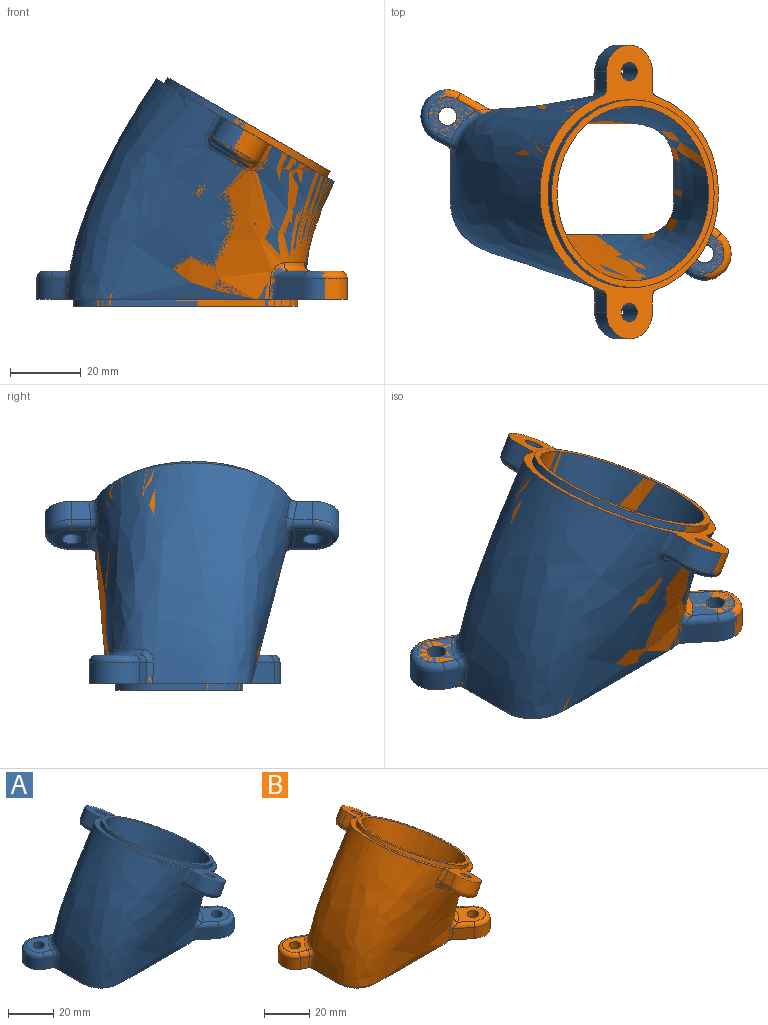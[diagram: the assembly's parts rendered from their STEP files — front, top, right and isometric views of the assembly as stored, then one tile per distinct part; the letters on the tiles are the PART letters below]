
ASSEMBLY  parts=2 mates=1
PART A: 60 faces, bbox 97.4x92.8x76.8 mm
  f0: plane 53.03x45.93mm, normal (0.5,0,0.87), area 293.8mm2, adj f11,f27
  f1: bspline ~76.16x63.21mm, area 8862.1mm2, adj f24,f26,f34,f35,f36,f37,f38,f39
  f2: plane 5.83x5.2mm, normal (0.87,0,-0.5), area 30.9mm2, adj f4,f26,f49,f54
  f3: plane 5.36x5.2mm, normal (-0.87,0,0.5), area 29mm2, adj f4,f26,f47,f50
  f4: cylinder r=7.5mm len=15.99mm, axis (0.5,0,0.87), area 141.4mm2, adj f2,f3,f26,f48
  f5: cylinder r=2.6mm len=9.53mm, axis (0.5,0,0.87), area 130.7mm2, adj f22,f26
  f6: plane 5.52x5.2mm, normal (0.87,0,-0.5), area 31.9mm2, adj f7,f26,f46,f59
  f7: cylinder r=7.5mm len=15.99mm, axis (0.5,0,0.87), area 141.4mm2, adj f6,f8,f26,f45
  f8: plane 5.37x5.2mm, normal (-0.87,0,0.5), area 31.2mm2, adj f7,f26,f44,f55
  f9: cylinder r=2.6mm len=9.53mm, axis (0.5,0,0.87), area 130.7mm2, adj f23,f26
  f10: plane 63.35x35.92mm, normal (0,0,-1), area 399.7mm2, adj f11,f25
  f11: offset ~85.51x76.83mm, area 8770.6mm2, adj f0,f10
  f12: cylinder r=7.51mm len=14.2mm, axis (0,0,-1), area 143.3mm2, adj f13,f14,f24,f29
  f13: plane 8.14x6mm, normal (0.49,0.87,0), area 54.1mm2, adj f12,f24,f30,f39
  f14: plane 6x3.93mm, normal (-0.45,-0.89,0), area 24mm2, adj f12,f24,f28,f43
  f15: plane 13.81x12.29mm, normal (0,0,1), area 77.9mm2, adj f16,f28,f29,f30,f41
  f16: cylinder r=2.6mm len=8mm, axis (0,0,-1), area 130.7mm2, adj f15,f24
  f17: cylinder r=7.51mm len=13.34mm, axis (0,0,-1), area 141.5mm2, adj f18,f19,f24,f32
  f18: plane 8.09x6.55mm, normal (-0.63,-0.78,0), area 60.1mm2, adj f17,f24,f33,f38
  f19: plane 8.6x6.97mm, normal (0.63,0.78,0), area 66mm2, adj f17,f24,f31,f34
  f20: plane 14.76x14.58mm, normal (0,0,1), area 102.7mm2, adj f21,f31,f32,f33,f36
  f21: cylinder r=2.6mm len=8mm, axis (0,0,-1), area 130.7mm2, adj f20,f24
  f22: plane 11.25x9.54mm, normal (-0.5,0,-0.87), area 84.3mm2, adj f5,f47,f48,f49,f52
  f23: plane 10.44x9.54mm, normal (-0.5,0,-0.87), area 77mm2, adj f9,f44,f45,f46,f57
  f24: plane 89.41x55.64mm, normal (0,0,-1), area 808.4mm2, adj f1,f12,f13,f14,f16,f17,f18,f19
  f25: extruded ~63.32x35.88mm, area 368mm2, adj f10,f24
  f26: plane 84.51x51.89mm, normal (0.5,0,0.87), area 731mm2, adj f1,f2,f3,f4,f5,f6,f7,f8
  f27: cylinder r=26.5mm len=53mm, axis (0.5,0,0.87), area 333mm2, adj f0,f26
  f28: cylinder r=2mm len=4.84mm, axis (-0.89,0.45,0), area 13.4mm2, adj f14,f15,f29,f42
  f29: torus R=5.51mm, axis (0,0,-1), area 67.8mm2, adj f12,f15,f28,f30
  f30: cylinder r=2mm len=9.12mm, axis (0.87,-0.49,0), area 24.7mm2, adj f13,f15,f29,f40
  f31: cylinder r=2mm len=9.67mm, axis (0.78,-0.63,0), area 29.4mm2, adj f19,f20,f32,f35
  f32: torus R=5.51mm, axis (0,0,-1), area 66.9mm2, adj f17,f20,f31,f33
  f33: cylinder r=2mm len=8.72mm, axis (-0.78,0.63,0), area 26.4mm2, adj f18,f20,f32,f37
  f34: bspline ~10.34x2.04mm, area 11.2mm2, adj f1,f19,f24,f35
  f35: bspline ~5.56x4.86mm, area 13.1mm2, adj f1,f31,f34,f36
  f36: bspline ~12.8x10.83mm, area 35.7mm2, adj f1,f20,f35,f37
  f37: bspline ~5.44x4.81mm, area 12.7mm2, adj f1,f33,f36,f38
  f38: bspline ~15.3x3.59mm, area 12mm2, adj f1,f18,f24,f37
  f39: bspline ~15.1x2.96mm, area 7.8mm2, adj f1,f13,f24,f40
  f40: bspline ~5.57x4.55mm, area 10.3mm2, adj f1,f30,f39,f41
  f41: bspline ~11.52x10.24mm, area 28.8mm2, adj f1,f15,f40,f42
  f42: bspline ~4.32x4.1mm, area 10.5mm2, adj f1,f28,f41,f43
  f43: bspline ~10.68x2.51mm, area 13.8mm2, adj f1,f14,f24,f42
  f44: cylinder r=2mm len=5.37mm, axis (0,-1,0), area 16mm2, adj f8,f23,f45,f56
  f45: torus R=5.5mm, axis (0.5,0,0.87), area 66.8mm2, adj f7,f23,f44,f46
  f46: cylinder r=2mm len=5.52mm, axis (0,1,0), area 16.4mm2, adj f6,f23,f45,f58
  f47: cylinder r=2mm len=5.36mm, axis (0,-1,0), area 16.8mm2, adj f3,f22,f48,f51
  f48: torus R=5.5mm, axis (0.5,0,0.87), area 66.8mm2, adj f4,f22,f47,f49
  f49: cylinder r=2mm len=5.83mm, axis (0,1,0), area 18.2mm2, adj f2,f22,f48,f53
  f50: bspline ~11.17x7.17mm, area 15.3mm2, adj f1,f3,f26,f51
  f51: bspline ~6.34x3.07mm, area 11.3mm2, adj f1,f47,f50,f52
  f52: bspline ~17.13x10.74mm, area 29mm2, adj f1,f22,f51,f53
  f53: bspline ~6.33x3.25mm, area 11.2mm2, adj f1,f49,f52,f54
  f54: bspline ~14.09x9.17mm, area 15.1mm2, adj f1,f2,f26,f53
  f55: bspline ~10.93x7.13mm, area 15.3mm2, adj f1,f8,f26,f56
  f56: bspline ~6.35x3.17mm, area 11.9mm2, adj f1,f44,f55,f57
  f57: bspline ~17.51x11.2mm, area 31.8mm2, adj f1,f23,f56,f58
  f58: bspline ~6.29x3.27mm, area 11.9mm2, adj f1,f46,f57,f59
  f59: bspline ~20.66x12.71mm, area 15.2mm2, adj f1,f6,f26,f58
PART B: 60 faces, bbox 97.4x92.8x76.8 mm
  f0: plane 53.03x45.93mm, normal (0.5,0,0.87), area 293.8mm2, adj f11,f27
  f1: bspline ~76.16x63.21mm, area 8862.1mm2, adj f24,f26,f34,f35,f36,f37,f38,f39
  f2: plane 5.83x5.2mm, normal (0.87,0,-0.5), area 30.9mm2, adj f4,f26,f49,f54
  f3: plane 5.36x5.2mm, normal (-0.87,0,0.5), area 29mm2, adj f4,f26,f47,f50
  f4: cylinder r=7.5mm len=15.99mm, axis (0.5,0,0.87), area 141.4mm2, adj f2,f3,f26,f48
  f5: cylinder r=2.6mm len=9.53mm, axis (0.5,0,0.87), area 130.7mm2, adj f22,f26
  f6: plane 5.52x5.2mm, normal (0.87,0,-0.5), area 31.9mm2, adj f7,f26,f46,f59
  f7: cylinder r=7.5mm len=15.99mm, axis (0.5,0,0.87), area 141.4mm2, adj f6,f8,f26,f45
  f8: plane 5.37x5.2mm, normal (-0.87,0,0.5), area 31.2mm2, adj f7,f26,f44,f55
  f9: cylinder r=2.6mm len=9.53mm, axis (0.5,0,0.87), area 130.7mm2, adj f23,f26
  f10: plane 63.35x35.92mm, normal (0,0,-1), area 399.7mm2, adj f11,f25
  f11: offset ~85.51x76.83mm, area 8770.6mm2, adj f0,f10
  f12: cylinder r=7.51mm len=14.2mm, axis (0,0,-1), area 143.3mm2, adj f13,f14,f24,f29
  f13: plane 8.14x6mm, normal (0.49,0.87,0), area 54.1mm2, adj f12,f24,f30,f39
  f14: plane 6x3.93mm, normal (-0.45,-0.89,0), area 24mm2, adj f12,f24,f28,f43
  f15: plane 13.81x12.29mm, normal (0,0,1), area 77.9mm2, adj f16,f28,f29,f30,f41
  f16: cylinder r=2.6mm len=8mm, axis (0,0,-1), area 130.7mm2, adj f15,f24
  f17: cylinder r=7.51mm len=13.34mm, axis (0,0,-1), area 141.5mm2, adj f18,f19,f24,f32
  f18: plane 8.09x6.55mm, normal (-0.63,-0.78,0), area 60.1mm2, adj f17,f24,f33,f38
  f19: plane 8.6x6.97mm, normal (0.63,0.78,0), area 66mm2, adj f17,f24,f31,f34
  f20: plane 14.76x14.58mm, normal (0,0,1), area 102.7mm2, adj f21,f31,f32,f33,f36
  f21: cylinder r=2.6mm len=8mm, axis (0,0,-1), area 130.7mm2, adj f20,f24
  f22: plane 11.25x9.54mm, normal (-0.5,0,-0.87), area 84.3mm2, adj f5,f47,f48,f49,f52
  f23: plane 10.44x9.54mm, normal (-0.5,0,-0.87), area 77mm2, adj f9,f44,f45,f46,f57
  f24: plane 89.41x55.64mm, normal (0,0,-1), area 808.4mm2, adj f1,f12,f13,f14,f16,f17,f18,f19
  f25: extruded ~63.32x35.88mm, area 368mm2, adj f10,f24
  f26: plane 84.51x51.89mm, normal (0.5,0,0.87), area 731mm2, adj f1,f2,f3,f4,f5,f6,f7,f8
  f27: cylinder r=26.5mm len=53mm, axis (0.5,0,0.87), area 333mm2, adj f0,f26
  f28: cylinder r=2mm len=4.84mm, axis (-0.89,0.45,0), area 13.4mm2, adj f14,f15,f29,f42
  f29: torus R=5.51mm, axis (0,0,-1), area 67.8mm2, adj f12,f15,f28,f30
  f30: cylinder r=2mm len=9.12mm, axis (0.87,-0.49,0), area 24.7mm2, adj f13,f15,f29,f40
  f31: cylinder r=2mm len=9.67mm, axis (0.78,-0.63,0), area 29.4mm2, adj f19,f20,f32,f35
  f32: torus R=5.51mm, axis (0,0,-1), area 66.9mm2, adj f17,f20,f31,f33
  f33: cylinder r=2mm len=8.72mm, axis (-0.78,0.63,0), area 26.4mm2, adj f18,f20,f32,f37
  f34: bspline ~10.34x2.04mm, area 11.2mm2, adj f1,f19,f24,f35
  f35: bspline ~5.56x4.86mm, area 13.1mm2, adj f1,f31,f34,f36
  f36: bspline ~12.8x10.83mm, area 35.7mm2, adj f1,f20,f35,f37
  f37: bspline ~5.44x4.81mm, area 12.7mm2, adj f1,f33,f36,f38
  f38: bspline ~15.3x3.59mm, area 12mm2, adj f1,f18,f24,f37
  f39: bspline ~15.1x2.96mm, area 7.8mm2, adj f1,f13,f24,f40
  f40: bspline ~5.57x4.55mm, area 10.3mm2, adj f1,f30,f39,f41
  f41: bspline ~11.52x10.24mm, area 28.8mm2, adj f1,f15,f40,f42
  f42: bspline ~4.32x4.1mm, area 10.5mm2, adj f1,f28,f41,f43
  f43: bspline ~10.68x2.51mm, area 13.8mm2, adj f1,f14,f24,f42
  f44: cylinder r=2mm len=5.37mm, axis (0,-1,0), area 16mm2, adj f8,f23,f45,f56
  f45: torus R=5.5mm, axis (0.5,0,0.87), area 66.8mm2, adj f7,f23,f44,f46
  f46: cylinder r=2mm len=5.52mm, axis (0,1,0), area 16.4mm2, adj f6,f23,f45,f58
  f47: cylinder r=2mm len=5.36mm, axis (0,-1,0), area 16.8mm2, adj f3,f22,f48,f51
  f48: torus R=5.5mm, axis (0.5,0,0.87), area 66.8mm2, adj f4,f22,f47,f49
  f49: cylinder r=2mm len=5.83mm, axis (0,1,0), area 18.2mm2, adj f2,f22,f48,f53
  f50: bspline ~11.17x7.17mm, area 15.3mm2, adj f1,f3,f26,f51
  f51: bspline ~6.34x3.07mm, area 11.3mm2, adj f1,f47,f50,f52
  f52: bspline ~17.13x10.74mm, area 29mm2, adj f1,f22,f51,f53
  f53: bspline ~6.33x3.25mm, area 11.2mm2, adj f1,f49,f52,f54
  f54: bspline ~14.09x9.17mm, area 15.1mm2, adj f1,f2,f26,f53
  f55: bspline ~10.93x7.13mm, area 15.3mm2, adj f1,f8,f26,f56
  f56: bspline ~6.35x3.17mm, area 11.9mm2, adj f1,f44,f55,f57
  f57: bspline ~17.51x11.2mm, area 31.8mm2, adj f1,f23,f56,f58
  f58: bspline ~6.29x3.27mm, area 11.9mm2, adj f1,f46,f57,f59
  f59: bspline ~20.66x12.71mm, area 15.2mm2, adj f1,f6,f26,f58
PLACE A t=(-38.85,131.97,-75.76)mm
PLACE B t=(-38.85,-91.55,-75.76)mm
MATE fastened A.f27 <-> B.f27  axis (0.5,0,0.87) through (60.42,3.3,-14.33)mm
